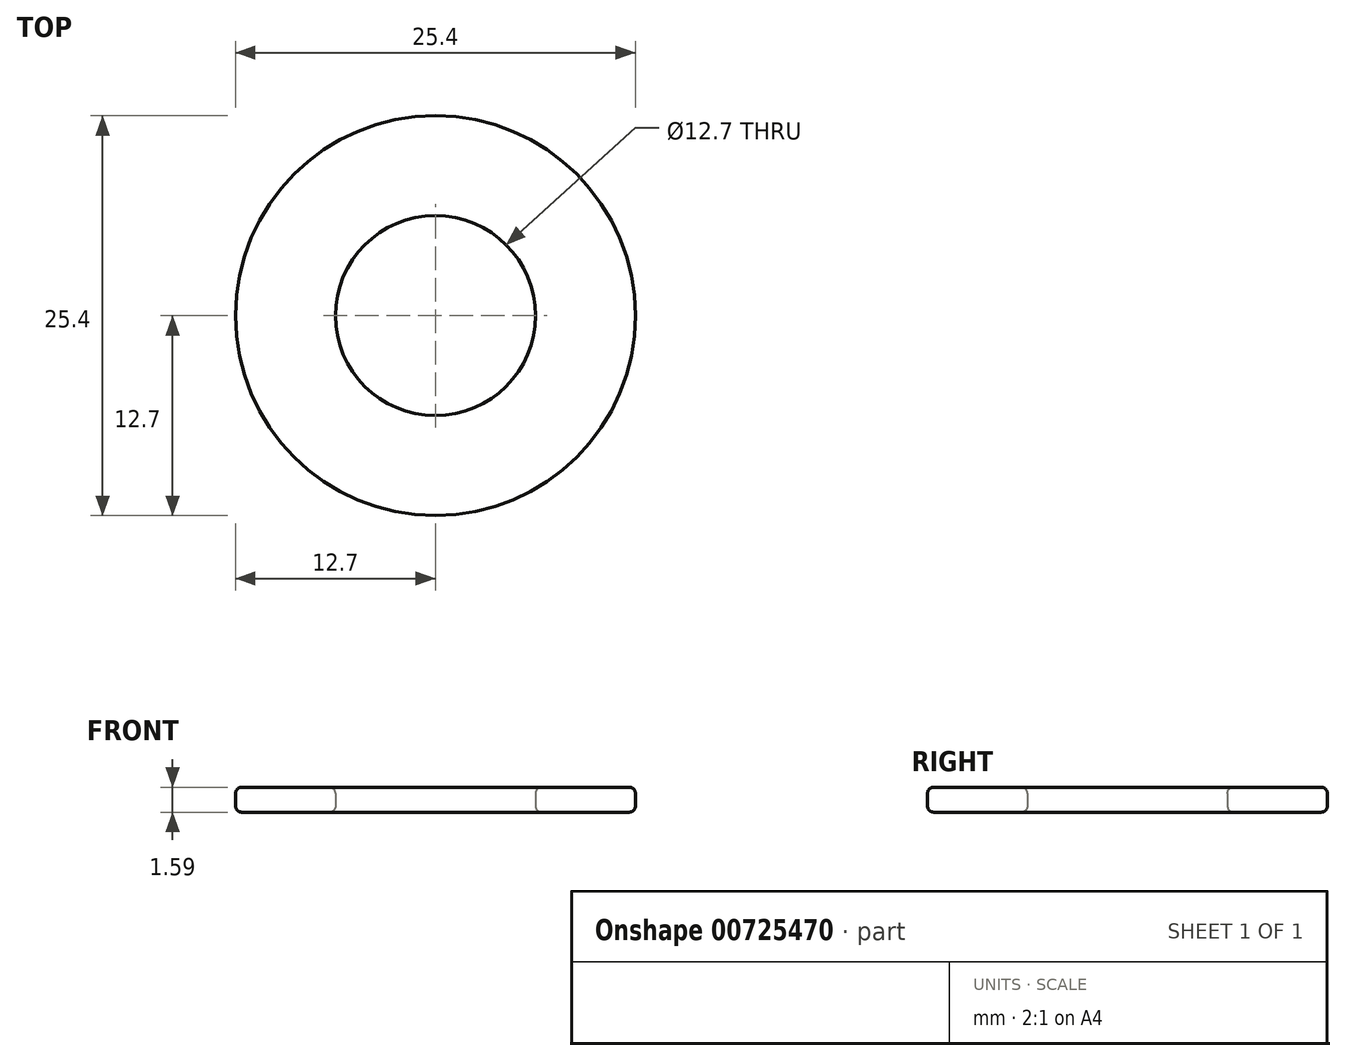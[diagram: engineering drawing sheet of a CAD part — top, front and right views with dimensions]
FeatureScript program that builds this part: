
annotation { "Feature Type Name" : "Feature", "Feature Type Description" : "" }
export const myFeature = defineFeature(function(context is Context, id is Id, definition is map)
    precondition{}
    {
        {
            var Q0;
            Q0=qCreatedBy(makeId("Top.planeOp"),FACE);
            var sketch = newSketch(context, id + "F0", { "sketchPlane" : qUnion([Q0])});
            skCircle(sketch, "E0", {"center": v(0, 0) * mm, "radius": 12.7 * mm});
            skCircle(sketch, "E1", {"center": v(0, 0) * mm, "radius": 6.35 * mm});
            skSolve(sketch);
        }
        {
            var Q0;
            Q0=makeQuery(id+"F0.imprint","IMPRINT",FACE,{"disambiguationData":[TD([[makeQuery(id+"F0.imprint","IMPRINT",EDGE,{"derivedFrom":sQuery(id+"F0.wireOp",EDGE,"E0")}),1.0]])]});
            extrude(context, id + "F1", {"entities" : qUnion([Q0]), "depth" : 1.59 * mm, "offsetDistance" : 25.4 * mm});
        }
        {
            var Q0;
            Q0=makeQuery(id+"F1.opExtrude","CAP_EDGE",EDGE,{"disambiguationData":[OSD([sQuery(id+"F0.wireOp",EDGE,"E0")])],"isStart":true});
            var Q1;
            Q1=makeQuery(id+"F1.opExtrude","CAP_EDGE",EDGE,{"disambiguationData":[OSD([sQuery(id+"F0.wireOp",EDGE,"E1")])],"isStart":true});
            var Q2;
            Q2=makeQuery(id+"F1.opExtrude","CAP_FACE",FACE,{"disambiguationData":[OSD([sQuery(id+"F0.wireOp",EDGE,"E0"),sQuery(id+"F0.wireOp",EDGE,"E1")])],"isStart":true});
            var Q3;
            Q3=makeQuery(id+"F1.opExtrude","CAP_EDGE",EDGE,{"disambiguationData":[OSD([sQuery(id+"F0.wireOp",EDGE,"E0")])],"isStart":false});
            var Q4;
            Q4=makeQuery(id+"F1.opExtrude","SWEPT_FACE",FACE,{"disambiguationData":[OSD([sQuery(id+"F0.wireOp",EDGE,"E0")])]});
            var Q5;
            Q5=makeQuery(id+"F1.opExtrude","CAP_FACE",FACE,{"disambiguationData":[OSD([sQuery(id+"F0.wireOp",EDGE,"E0"),sQuery(id+"F0.wireOp",EDGE,"E1")])],"isStart":false});
            var Q6;
            Q6=makeQuery(id+"F1.opExtrude","CAP_EDGE",EDGE,{"disambiguationData":[OSD([sQuery(id+"F0.wireOp",EDGE,"E1")])],"isStart":false});
            var Q7;
            Q7=makeQuery(id+"F1.opExtrude","SWEPT_FACE",FACE,{"disambiguationData":[OSD([sQuery(id+"F0.wireOp",EDGE,"E1")])]});
            fillet(context, id + "F2", {"entities" : qUnion([Q0, Q1, Q2, Q3, Q4, Q5, Q6, Q7]), "radius" : 0.4 * mm, "tangentPropagation" : true, "allowEdgeOverflow" : false});
        }
    });
